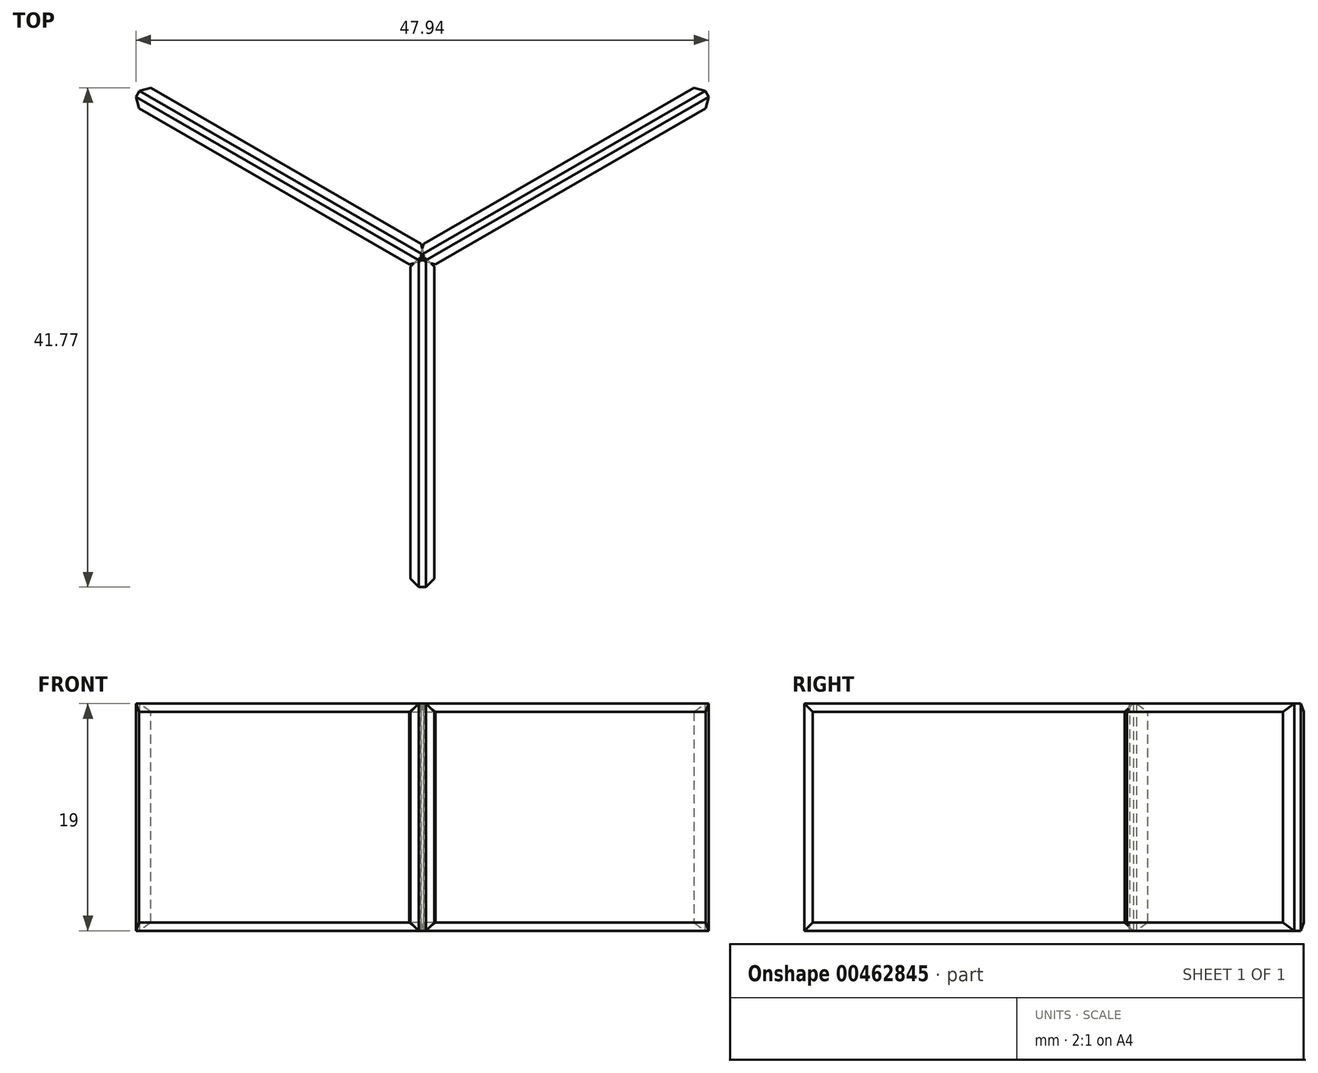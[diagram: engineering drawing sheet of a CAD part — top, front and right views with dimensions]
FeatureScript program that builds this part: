
annotation { "Feature Type Name" : "Feature", "Feature Type Description" : "" }
export const myFeature = defineFeature(function(context is Context, id is Id, definition is map)
    precondition{}
    {
        {
            var Q0;
            Q0=qCreatedBy(makeId("Top.planeOp"),FACE);
            var sketch = newSketch(context, id + "F0", { "sketchPlane" : qUnion([Q0])});
            skLineSegment(sketch, "E0.bottom", {"start": v(0, 0) * mm, "end": v(-2, 0) * mm});
            skLineSegment(sketch, "E0.top", {"start": v(0, 27.5) * mm, "end": v(-2, 27.5) * mm});
            skLineSegment(sketch, "E0.left", {"start": v(0, 0) * mm, "end": v(0, 27.5) * mm});
            skLineSegment(sketch, "E0.right", {"start": v(-2, 0) * mm, "end": v(-2, 27.5) * mm});
            skLineSegment(sketch, "E1", {"start": v(0, 0) * mm, "end": v(13.96, 0) * mm});
            skLineSegment(sketch, "E2", {"start": v(18.5, 0) * mm, "end": v(26.01, 0) * mm});
            skSolve(sketch);
        }
        {
            var Q0;
            Q0=makeQuery(id+"F0.imprint","IMPRINT",FACE,{"disambiguationData":[TD([[makeQuery(id+"F0.imprint","IMPRINT",EDGE,{"derivedFrom":sQuery(id+"F0.wireOp",EDGE,"E0.bottom")}),-1.0]])]});
            extrude(context, id + "F1", {"entities" : qUnion([Q0]), "depth" : 19 * mm});
        }
        {
            var Q0;
            Q0=qCreatedBy(makeId("Top.planeOp"),FACE);
            var sketch = newSketch(context, id + "F2", { "sketchPlane" : qUnion([Q0])});
            skLineSegment(sketch, "E3", {"start": v(13.67, 0) * mm, "end": v(36.23, 0) * mm});
            skSolve(sketch);
        }
        {
            var Q0;
            Q0=makeQuery(id+"F1.opExtrude","SWEPT_BODY",BODY,{"disambiguationData":[OSD([sQuery(id+"F0.wireOp",EDGE,"E0.bottom"),sQuery(id+"F0.wireOp",EDGE,"E0.top"),sQuery(id+"F0.wireOp",EDGE,"E0.left"),sQuery(id+"F0.wireOp",EDGE,"E0.right")])]});
            var Q1;
            Q1=sQuery(id+"F2.wireOp",EDGE,"E3");
            transform(context, id + "F3", {"entities" : qUnion([Q0]), "transformType" : TransformType.TRANSLATION_DISTANCE, "transformDirection" : qUnion([Q1]), "distance" : 1 * mm, "makeCopy" : false});
        }
        {
            var Q0;
            Q0=qCreatedBy(makeId("Top.planeOp"),FACE);
            var sketch = newSketch(context, id + "F4", { "sketchPlane" : qUnion([Q0])});
            skLineSegment(sketch, "E4", {"start": v(0, 62.06) * mm, "end": v(0, 72.35) * mm});
            skSolve(sketch);
        }
        {
            var Q0;
            Q0=makeQuery(id+"F1.opExtrude","SWEPT_BODY",BODY,{"disambiguationData":[OSD([sQuery(id+"F0.wireOp",EDGE,"E0.bottom"),sQuery(id+"F0.wireOp",EDGE,"E0.top"),sQuery(id+"F0.wireOp",EDGE,"E0.left"),sQuery(id+"F0.wireOp",EDGE,"E0.right")])]});
            var Q1;
            Q1=sQuery(id+"F4.wireOp",EDGE,"E4");
            transform(context, id + "F5", {"entities" : qUnion([Q0]), "transformType" : TransformType.TRANSLATION_DISTANCE, "transformDirection" : qUnion([Q1]), "distance" : 27.5 * mm, "oppositeDirection" : true, "makeCopy" : false});
        }
        {
            var Q0;
            Q0=qCreatedBy(makeId("Front.planeOp"),FACE);
            var sketch = newSketch(context, id + "F6", { "sketchPlane" : qUnion([Q0])});
            skLineSegment(sketch, "E5", {"start": v(0, 0) * mm, "end": v(0, 39.05) * mm});
            skSolve(sketch);
        }
        {
            var Q0;
            Q0=makeQuery(id+"F1.opExtrude","SWEPT_BODY",BODY,{"disambiguationData":[OSD([sQuery(id+"F0.wireOp",EDGE,"E0.bottom"),sQuery(id+"F0.wireOp",EDGE,"E0.top"),sQuery(id+"F0.wireOp",EDGE,"E0.left"),sQuery(id+"F0.wireOp",EDGE,"E0.right")])]});
            var Q1;
            Q1=sQuery(id+"F6.wireOp",EDGE,"E5");
            circularPattern(context, id + "F7", {"entities" : qUnion([Q0]), "axis" : qUnion([Q1]), "angle" : 360 * degree, "instanceCount" : 3, "equalSpace" : true});
        }
        {
            var Q0;
            Q0=makeQuery(id+"F1.opExtrude","SWEPT_FACE",FACE,{"disambiguationData":[OSD([sQuery(id+"F0.wireOp",EDGE,"E0.left")])]});
            var Q1;
            Q1=makeQuery(id+"F7.opPattern","COPY",FACE,{"derivedFrom":makeQuery(id+"F1.opExtrude","SWEPT_FACE",FACE,{"disambiguationData":[OSD([sQuery(id+"F0.wireOp",EDGE,"E0.left")])]}),"instanceName":"1"});
            var Q2;
            Q2=makeQuery(id+"F7.opPattern","COPY",FACE,{"derivedFrom":makeQuery(id+"F1.opExtrude","SWEPT_FACE",FACE,{"disambiguationData":[OSD([sQuery(id+"F0.wireOp",EDGE,"E0.left")])]}),"instanceName":"2"});
            var Q3;
            Q3=makeQuery(id+"F7.opPattern","COPY",FACE,{"derivedFrom":makeQuery(id+"F1.opExtrude","SWEPT_FACE",FACE,{"disambiguationData":[OSD([sQuery(id+"F0.wireOp",EDGE,"E0.right")])]}),"instanceName":"2"});
            var Q4;
            Q4=makeQuery(id+"F7.opPattern","COPY",FACE,{"derivedFrom":makeQuery(id+"F1.opExtrude","SWEPT_FACE",FACE,{"disambiguationData":[OSD([sQuery(id+"F0.wireOp",EDGE,"E0.right")])]}),"instanceName":"1"});
            var Q5;
            Q5=makeQuery(id+"F1.opExtrude","SWEPT_FACE",FACE,{"disambiguationData":[OSD([sQuery(id+"F0.wireOp",EDGE,"E0.right")])]});
            chamfer(context, id + "F8", {"entities" : qUnion([Q0, Q1, Q2, Q3, Q4, Q5]), "width" : 0.7 * mm, "tangentPropagation" : true});
        }
    });
